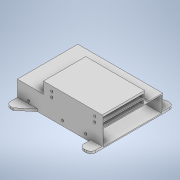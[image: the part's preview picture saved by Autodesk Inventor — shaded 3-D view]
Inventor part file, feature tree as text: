
AUTODESK INVENTOR PART (.ipt)
format: ipt  version: 2022 (Build 260153000, 153)  size: 235,008 bytes
history: native  units: mm
features: extrude x5, sketch x5, fillet x1
ambient origin geometry x8: Origin, YZ Plane, XZ Plane, XY Plane, X Axis, Y Axis, Z Axis, Center Point
bodies: Solid1 (feature_tree)
feature tree (11):
  extrude  "Extrusion1"  Depth=150.0mm
  extrude  "Extrusion2"  Depth=104.0mm
  extrude  "Extrusion3"  Depth=20.0mm TaperAngle=0.0deg
  extrude  "Extrusion4"  Depth=20.0mm
  fillet  "Fillet1"  Radius=20.0mm
  extrude  "Extrusion5"  Depth=2.0mm
  sketch  "Sketch1"  dims[d0=107.0mm d1=150.0mm]
  sketch  "Sketch3"  dims[d2=32.0mm d3=0.0mm d4=104.0mm]
  sketch  "Sketch4"  dims[d5=75.0mm d6=20.0mm d7=0.0mm]
  sketch  "Sketch5"  dims[d8=20.0mm d9=20.0mm d10=20.0mm]
  sketch  "Sketch6"  dims[d11=20.0mm d15=8.0mm d17=6.981317mm d18=1.0mm d19=6.981317mm d20=1.0mm d21=4.0mm d22=0.0mm d23=7.0mm d24=7.0mm d25=28.0mm d26=71.0mm d27=71.0mm d28=2.0mm d29=2.0mm d31=2.0mm d32=2.0mm d33=103.0mm d34=2.0mm d35=1000.0mm d36=0.0mm d37=8.0mm d38=29.0mm d39=41.0mm d40=0.0mm d42=0.0mm d43=60.0mm d44=4.0mm d45=4.0mm d46=4.0mm d47=8.5mm d48=0.0mm d49=76.0mm d50=15.0mm d51=4.0mm d52=4.0mm d53=2.5mm d54=4.0mm d55=4.0mm d56=2.5mm d57=2.5mm d58=1000.0mm d59=0.0mm]
